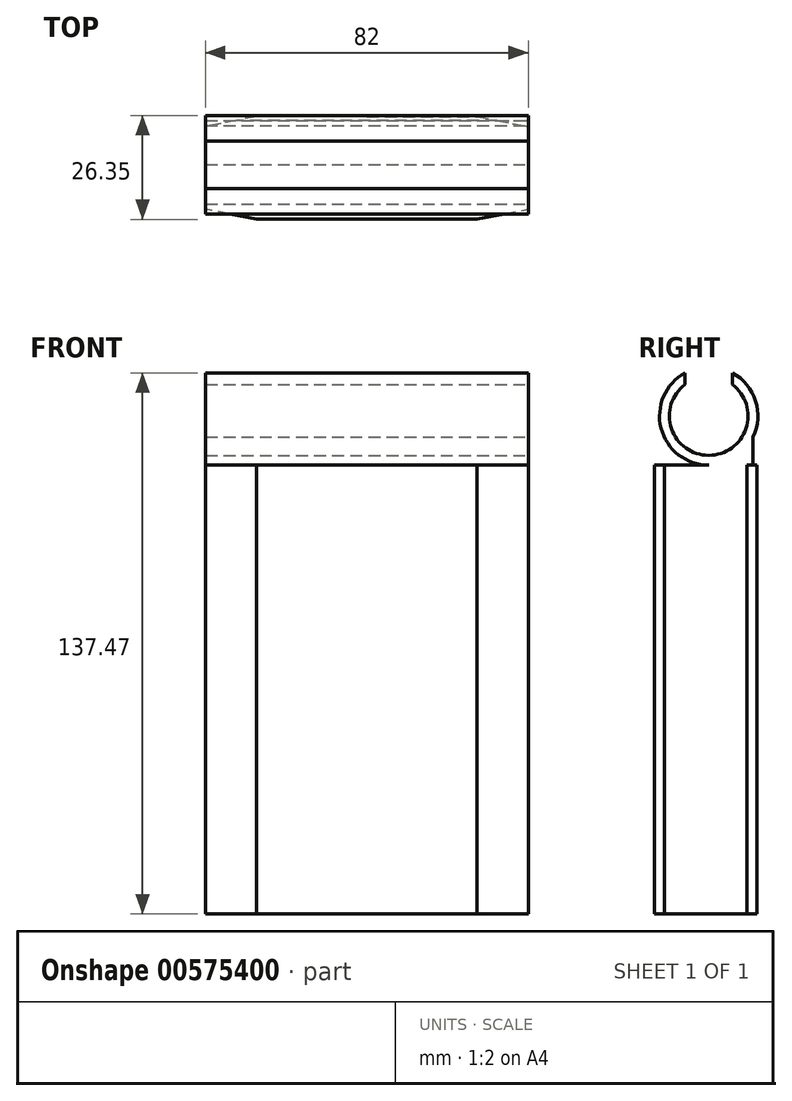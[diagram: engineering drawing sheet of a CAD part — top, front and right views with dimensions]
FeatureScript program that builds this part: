
annotation { "Feature Type Name" : "Feature", "Feature Type Description" : "" }
export const myFeature = defineFeature(function(context is Context, id is Id, definition is map)
    precondition{}
    {
        {
            var Q0;
            Q0=qCreatedBy(makeId("Top.planeOp"),FACE);
            var sketch = newSketch(context, id + "F0", { "sketchPlane" : qUnion([Q0])});
            skPoint(sketch, "E0", {"position": v(-66.3, -0.78) * mm});
            skPoint(sketch, "E1", {"position": v(-56.62, -0.78) * mm});
            skPoint(sketch, "E2", {"position": v(25.38, -0.78) * mm});
            skLineSegment(sketch, "E3", {"start": v(25.38, -0.78) * mm, "end": v(-56.62, -0.78) * mm});
            skLineSegment(sketch, "E4", {"start": v(25.38, -0.78) * mm, "end": v(35.38, -0.78) * mm});
            skLineSegment(sketch, "E5", {"start": v(-56.62, -0.78) * mm, "end": v(-70.62, -0.78) * mm});
            skLineSegment(sketch, "E6.bottom", {"start": v(-56.62, 9.72) * mm, "end": v(25.38, 9.72) * mm});
            skLineSegment(sketch, "E6.top", {"start": v(-56.62, -11.28) * mm, "end": v(25.38, -11.28) * mm});
            skLineSegment(sketch, "E6.left", {"start": v(-56.62, 9.72) * mm, "end": v(-56.62, -11.28) * mm});
            skLineSegment(sketch, "E6.right", {"start": v(25.38, 9.72) * mm, "end": v(25.38, -11.28) * mm});
            skPoint(sketch, "E6.middle", {"position": v(-15.62, -0.78) * mm});
            skLineSegment(sketch, "E7.bottom", {"start": v(-70.62, 15.22) * mm, "end": v(26.49, 15.22) * mm});
            skLineSegment(sketch, "E7.top", {"start": v(-70.62, -16.78) * mm, "end": v(26.49, -16.78) * mm});
            skLineSegment(sketch, "E7.left", {"start": v(-70.62, 15.22) * mm, "end": v(-70.62, -16.78) * mm});
            skLineSegment(sketch, "E8", {"start": v(35.38, -0.78) * mm, "end": v(30.38, -0.78) * mm});
            skLineSegment(sketch, "E9", {"start": v(35.38, -0.78) * mm, "end": v(35.38, 11.22) * mm});
            skLineSegment(sketch, "E10", {"start": v(35.38, 11.22) * mm, "end": v(35.38, -12.78) * mm});
            skLineSegment(sketch, "E11", {"start": v(35.38, -0.78) * mm, "end": v(28.2, -0.78) * mm});
            skLineSegment(sketch, "E12", {"start": v(35.38, -0.78) * mm, "end": v(35.38, 9.22) * mm});
            skLineSegment(sketch, "E13", {"start": v(35.38, 9.22) * mm, "end": v(35.38, 11.22) * mm});
            skLineSegment(sketch, "E14", {"start": v(35.38, 11.22) * mm, "end": v(29.38, 12.31) * mm});
            skLineSegment(sketch, "E15", {"start": v(29.38, 12.31) * mm, "end": v(29.38, 14.13) * mm});
            skLineSegment(sketch, "E16", {"start": v(29.38, 14.13) * mm, "end": v(26.49, 15.22) * mm});
            skPoint(sketch, "E17.end.orphan", {"position": v(29.38, 15.22) * mm});
            skLineSegment(sketch, "E18", {"start": v(-16.03, 12.22) * mm, "end": v(12.38, 12.28) * mm});
            skLineSegment(sketch, "E19", {"start": v(12.38, 12.28) * mm, "end": v(25.38, 9.72) * mm});
            skPoint(sketch, "E20.start.orphan", {"position": v(25.38, 12.31) * mm});
            skLineSegment(sketch, "E21.MirrorCS", {"start": v(-16.03, -13.78) * mm, "end": v(12.38, -13.85) * mm});
            skLineSegment(sketch, "E22.MirrorCS", {"start": v(12.38, -13.85) * mm, "end": v(25.38, -11.28) * mm});
            skLineSegment(sketch, "E23.MirrorCS", {"start": v(29.38, -15.7) * mm, "end": v(26.49, -16.78) * mm});
            skLineSegment(sketch, "E24.MirrorCS", {"start": v(35.38, -12.78) * mm, "end": v(29.38, -13.87) * mm});
            skLineSegment(sketch, "E25.MirrorCS", {"start": v(29.38, -13.87) * mm, "end": v(29.38, -15.7) * mm});
            skLineSegment(sketch, "E26.MirrorCS", {"start": v(35.38, -10.78) * mm, "end": v(35.38, -12.78) * mm});
            skLineSegment(sketch, "E27.MirrorCS", {"start": v(35.38, -0.78) * mm, "end": v(35.38, -10.78) * mm});
            skLineSegment(sketch, "E28", {"start": v(-56.62, -0.78) * mm, "end": v(25.38, -0.78) * mm});
            skLineSegment(sketch, "E29", {"start": v(-15.62, -0.78) * mm, "end": v(-15.62, -6.93) * mm});
            skLineSegment(sketch, "E30.MirrorCS", {"start": v(-15.22, -13.78) * mm, "end": v(-43.62, -13.85) * mm});
            skLineSegment(sketch, "E31.MirrorCS", {"start": v(-43.62, -13.85) * mm, "end": v(-56.62, -11.28) * mm});
            skLineSegment(sketch, "E32.MirrorCS", {"start": v(-43.62, 12.28) * mm, "end": v(-56.62, 9.72) * mm});
            skLineSegment(sketch, "E33.MirrorCS", {"start": v(-15.22, 12.22) * mm, "end": v(-43.62, 12.28) * mm});
            skSolve(sketch);
        }
        {
            var Q0;
            Q0=makeQuery(id+"F0.imprint","IMPRINT",FACE,{"disambiguationData":[TD([[makeQuery(id+"F0.imprint","IMPRINT",EDGE,{"derivedFrom":sQuery(id+"F0.wireOp",EDGE,"E6.bottom")}),1.0]])]});
            var Q1;
            {var subQ6=sQuery(id+"F0.wireOp",EDGE,"E6.bottom");Q1=makeQuery(id+"F0.imprint","IMPRINT",FACE,{"disambiguationData":[TD([[makeQuery(id+"F0.imprint","IMPRINT",EDGE,{"derivedFrom":subQ6}),-1.0]])]});}
            var Q2;
            {var subQ3=sQuery(id+"F0.wireOp",EDGE,"E6.top");Q2=makeQuery(id+"F0.imprint","IMPRINT",FACE,{"disambiguationData":[TD([[makeQuery(id+"F0.imprint","IMPRINT",EDGE,{"derivedFrom":subQ3}),1.0]])]});}
            var Q3;
            Q3=makeQuery(id+"F0.imprint","IMPRINT",FACE,{"disambiguationData":[TD([[makeQuery(id+"F0.imprint","IMPRINT",EDGE,{"derivedFrom":sQuery(id+"F0.wireOp",EDGE,"E6.top")}),-1.0]])]});
            extrude(context, id + "F1", {"entities" : qUnion([Q0, Q1, Q2, Q3]), "depth" : 114 * mm, "offsetDistance" : 25 * mm});
        }
        {
            var Q0;
            Q0=makeQuery(id+"F1.opExtrude","SWEPT_FACE",FACE,{"disambiguationData":[OSD([sQuery(id+"F0.wireOp",EDGE,"E6.right")])]});
            var sketch = newSketch(context, id + "F2", { "sketchPlane" : qUnion([Q0])});
            skLineSegment(sketch, "E34", {"start": v(0, 114) * mm, "end": v(0, 139) * mm});
            skCircle(sketch, "E35", {"center": v(0, 126.5) * mm, "radius": 12.5 * mm});
            skLineSegment(sketch, "E36.bottom", {"start": v(-11.28, 114) * mm, "end": v(11.28, 114) * mm});
            skLineSegment(sketch, "E36.top", {"start": v(-11.28, 139) * mm, "end": v(11.28, 139) * mm});
            skLineSegment(sketch, "E36.left", {"start": v(-11.28, 114) * mm, "end": v(-11.28, 139) * mm});
            skLineSegment(sketch, "E36.right", {"start": v(11.28, 114) * mm, "end": v(11.28, 139) * mm});
            skCircle(sketch, "E37.0", {"center": v(0, 126.5) * mm, "radius": 10 * mm});
            skLineSegment(sketch, "E38.bottom", {"start": v(-6, 134.5) * mm, "end": v(6, 134.5) * mm});
            skLineSegment(sketch, "E38.top", {"start": v(-6, 143.5) * mm, "end": v(6, 143.5) * mm});
            skLineSegment(sketch, "E38.left", {"start": v(-6, 134.5) * mm, "end": v(-6, 143.5) * mm});
            skLineSegment(sketch, "E38.right", {"start": v(6, 134.5) * mm, "end": v(6, 143.5) * mm});
            skPoint(sketch, "E38.middle", {"position": v(0, 139) * mm});
            skSolve(sketch);
        }
        {
            var Q0;
            {var subQ0=sQuery(id+"F2.wireOp",EDGE,"E36.left");var subQ1=sQuery(id+"F2.wireOp",EDGE,"E35");var subQ2=makeQuery(id+"F2.imprint","INTERSECT",VERTEX,{"disambiguationData":[OD(0.0)],"derivedFrom":[subQ1,subQ0]});Q0=makeQuery(id+"F2.imprint","IMPRINT",FACE,{"disambiguationData":[TD([[makeQuery(id+"F2.imprint","IMPRINT",EDGE,{"disambiguationData":[TD([[subQ2,-1.0]])],"derivedFrom":subQ1}),1.0]])]});}
            var Q1;
            {var subQ1=sQuery(id+"F2.wireOp",EDGE,"E35");var subQ3=sQuery(id+"F2.wireOp",EDGE,"E36.left");var subQ4=makeQuery(id+"F2.imprint","INTERSECT",VERTEX,{"disambiguationData":[OD(1.0)],"derivedFrom":[subQ1,subQ3]});Q1=makeQuery(id+"F2.imprint","IMPRINT",FACE,{"disambiguationData":[TD([[makeQuery(id+"F2.imprint","IMPRINT",EDGE,{"disambiguationData":[TD([[subQ4,-1.0]])],"derivedFrom":subQ1}),-1.0]])]});}
            var Q2;
            {var subQ0=sQuery(id+"F2.wireOp",EDGE,"E35");var subQ3=sQuery(id+"F2.wireOp",EDGE,"E36.left");var subQ5=makeQuery(id+"F2.imprint","INTERSECT",VERTEX,{"disambiguationData":[OD(0.0)],"derivedFrom":[subQ0,subQ3]});Q2=makeQuery(id+"F2.imprint","IMPRINT",FACE,{"disambiguationData":[TD([[makeQuery(id+"F2.imprint","IMPRINT",EDGE,{"disambiguationData":[TD([[subQ5,1.0]])],"derivedFrom":subQ0}),1.0]])]});}
            var Q3;
            {var subQ0=sQuery(id+"F2.wireOp",EDGE,"E36.right");var subQ1=sQuery(id+"F2.wireOp",EDGE,"E35");var subQ2=makeQuery(id+"F2.imprint","INTERSECT",VERTEX,{"disambiguationData":[OD(0.0)],"derivedFrom":[subQ1,subQ0]});Q3=makeQuery(id+"F2.imprint","IMPRINT",FACE,{"disambiguationData":[TD([[makeQuery(id+"F2.imprint","IMPRINT",EDGE,{"disambiguationData":[TD([[subQ2,-1.0]])],"derivedFrom":subQ1}),1.0]])]});}
            var Q4;
            {var subQ0=sQuery(id+"F2.wireOp",EDGE,"E36.bottom");var subQ3=sQuery(id+"F2.wireOp",EDGE,"E36.right");var subQ6=makeQuery(id+"F2.imprint","INTERSECT",VERTEX,{"derivedFrom":[subQ0,subQ3]});Q4=makeQuery(id+"F2.imprint","IMPRINT",FACE,{"disambiguationData":[TD([[makeQuery(id+"F2.imprint","IMPRINT",EDGE,{"disambiguationData":[TD([[subQ6,-1.0]])],"derivedFrom":subQ3}),1.0]])]});}
            var Q5;
            {var subQ0=sQuery(id+"F2.wireOp",EDGE,"E36.right");var subQ1=sQuery(id+"F2.wireOp",EDGE,"E35");var subQ2=makeQuery(id+"F2.imprint","INTERSECT",VERTEX,{"disambiguationData":[OD(0.0)],"derivedFrom":[subQ1,subQ0]});Q5=makeQuery(id+"F2.imprint","IMPRINT",FACE,{"disambiguationData":[TD([[makeQuery(id+"F2.imprint","IMPRINT",EDGE,{"disambiguationData":[TD([[subQ2,1.0]])],"derivedFrom":subQ1}),1.0]])]});}
            extrude(context, id + "F3", {"entities" : qUnion([Q0, Q1, Q2, Q3, Q4, Q5]), "operationType" : NewBodyOperationType.ADD, "oppositeDirection" : true, "depth" : 82 * mm, "offsetDistance" : 25 * mm});
        }
    });
